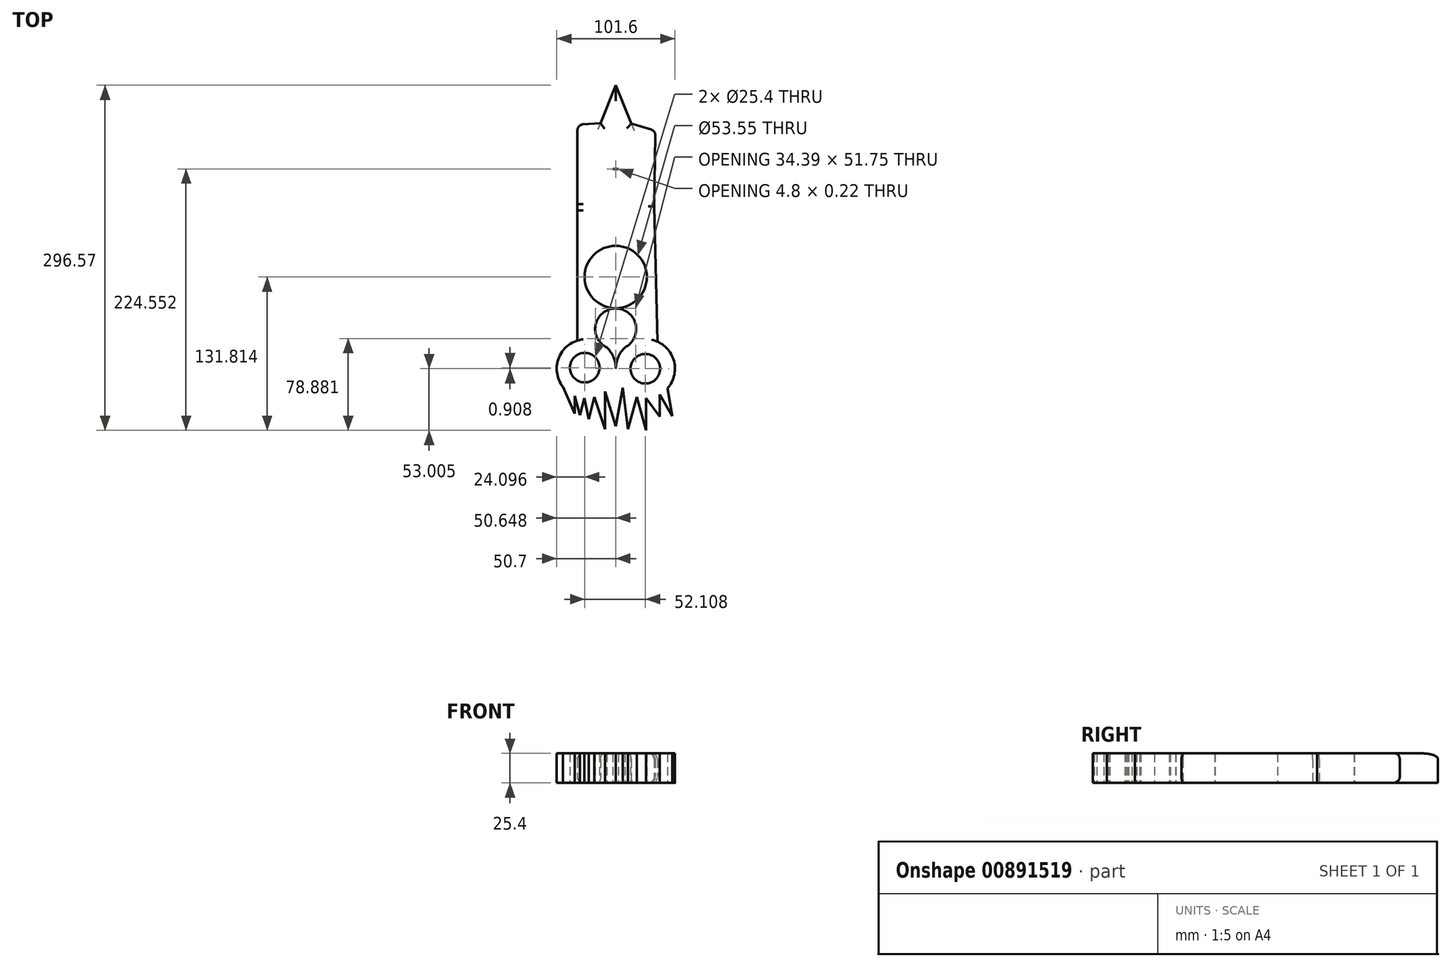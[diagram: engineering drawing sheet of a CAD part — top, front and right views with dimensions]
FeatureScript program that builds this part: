
annotation { "Feature Type Name" : "Feature", "Feature Type Description" : "" }
export const myFeature = defineFeature(function(context is Context, id is Id, definition is map)
    precondition{}
    {
        {
            var Q0;
            Q0=qCreatedBy(makeId("Top.planeOp"),FACE);
            var sketch = newSketch(context, id + "F0", { "sketchPlane" : qUnion([Q0])});
            skCircle(sketch, "E0", {"center": v(-25.3, -34.1) * mm, "radius": 25.4 * mm});
            skCircle(sketch, "E1", {"center": v(25.5, -34.1) * mm, "radius": 25.4 * mm});
            skLineSegment(sketch, "E2", {"start": v(-45.47, -49.53) * mm, "end": v(-35.26, -72.67) * mm});
            skLineSegment(sketch, "E3", {"start": v(-35.26, -72.67) * mm, "end": v(-35.26, -57.47) * mm});
            skLineSegment(sketch, "E4", {"start": v(-35.26, -57.47) * mm, "end": v(-30.65, -73.82) * mm});
            skLineSegment(sketch, "E5", {"start": v(-30.65, -73.82) * mm, "end": v(-27.09, -59.44) * mm});
            skLineSegment(sketch, "E6", {"start": v(-27.09, -59.44) * mm, "end": v(-23.17, -77.56) * mm});
            skLineSegment(sketch, "E7", {"start": v(-23.17, -77.56) * mm, "end": v(-18.39, -58.55) * mm});
            skLineSegment(sketch, "E8", {"start": v(-18.39, -58.55) * mm, "end": v(-9.07, -85.96) * mm});
            skLineSegment(sketch, "E9", {"start": v(-9.07, -85.96) * mm, "end": v(-9.07, -53.64) * mm});
            skLineSegment(sketch, "E10", {"start": v(-9.07, -53.64) * mm, "end": v(0, -83.66) * mm});
            skLineSegment(sketch, "E11", {"start": v(0, -83.66) * mm, "end": v(6.2, -50.61) * mm});
            skLineSegment(sketch, "E12", {"start": v(6.2, -50.61) * mm, "end": v(10.5, -85.96) * mm});
            skLineSegment(sketch, "E13", {"start": v(10.5, -85.96) * mm, "end": v(18.17, -58.42) * mm});
            skLineSegment(sketch, "E14", {"start": v(18.17, -58.42) * mm, "end": v(26.05, -87.11) * mm});
            skLineSegment(sketch, "E15", {"start": v(26.05, -87.11) * mm, "end": v(26.05, -59.5) * mm});
            skLineSegment(sketch, "E16", {"start": v(26.05, -59.5) * mm, "end": v(37.97, -75.12) * mm});
            skLineSegment(sketch, "E17", {"start": v(37.97, -75.12) * mm, "end": v(37.97, -56.24) * mm});
            skLineSegment(sketch, "E18", {"start": v(37.97, -56.24) * mm, "end": v(48.5, -75.02) * mm});
            skLineSegment(sketch, "E19", {"start": v(48.5, -75.02) * mm, "end": v(44.54, -50.92) * mm});
            skCircle(sketch, "E20", {"center": v(0, 0) * mm, "radius": 17.65 * mm});
            skCircle(sketch, "E21", {"center": v(0, 44.7) * mm, "radius": 26.78 * mm});
            skCircle(sketch, "E22", {"center": v(0, 104.57) * mm, "radius": 32.98 * mm});
            skCircle(sketch, "E23", {"center": v(0, 159.25) * mm, "radius": 21.92 * mm});
            skLineSegment(sketch, "E24", {"start": v(-32.86, 107.4) * mm, "end": v(-32.86, -9.86) * mm});
            skLineSegment(sketch, "E25", {"start": v(32.97, 105.4) * mm, "end": v(35.94, -10.95) * mm});
            skLineSegment(sketch, "E26", {"start": v(-13.07, 176.85) * mm, "end": v(0, 209.46) * mm});
            skLineSegment(sketch, "E27", {"start": v(0, 209.46) * mm, "end": v(13.46, 176.55) * mm});
            skLineSegment(sketch, "E28", {"start": v(-32.86, 107.4) * mm, "end": v(-32.86, 175.48) * mm});
            skLineSegment(sketch, "E29", {"start": v(-32.86, 175.48) * mm, "end": v(-13.07, 176.85) * mm});
            skLineSegment(sketch, "E30", {"start": v(13.46, 176.55) * mm, "end": v(34.1, 170.3) * mm});
            skLineSegment(sketch, "E31", {"start": v(34.1, 170.3) * mm, "end": v(32.97, 105.4) * mm});
            skSolve(sketch);
        }
        {
            var Q0;
            Q0 = qSketchRegion(id + "F0", true);
            extrude(context, id + "F1", {"entities" : qUnion([Q0]), "depth" : 25.4 * mm, "offsetDistance" : 25.4 * mm});
        }
        {
            var Q0;
            Q0=makeQuery(id+"F1.opExtrude","CAP_EDGE",EDGE,{"disambiguationData":[OSD([sQuery(id+"F0.wireOp",EDGE,"E31")])],"isStart":false});
            var Q1;
            Q1=makeQuery(id+"F1.opExtrude","CAP_EDGE",EDGE,{"disambiguationData":[OSD([sQuery(id+"F0.wireOp",EDGE,"E31")])],"isStart":true});
            fillet(context, id + "F2", {"entities" : qUnion([Q0, Q1]), "radius" : 5.08 * mm, "tangentPropagation" : true, "allowEdgeOverflow" : false});
        }
        {
            var Q0;
            {var subQ0=sQuery(id+"F0.wireOp",EDGE,"E24");var subQ1=sQuery(id+"F0.wireOp",EDGE,"E22");Q0=makeQuery(id+"F1.opExtrude","CAP_EDGE",EDGE,{"disambiguationData":[OSD([subQ1]),TDD([makeQuery(id+"F0.imprint","IMPRINT",EDGE,{"disambiguationData":[TD([[makeQuery(id+"F0.imprint","INTERSECT",VERTEX,{"derivedFrom":[subQ1,subQ0]}),1.0]])],"derivedFrom":subQ1})])],"isStart":false});}
            var Q1;
            {var subQ0=sQuery(id+"F0.wireOp",EDGE,"E24");var subQ1=sQuery(id+"F0.wireOp",EDGE,"E22");Q1=makeQuery(id+"F1.opExtrude","CAP_EDGE",EDGE,{"disambiguationData":[OSD([subQ1]),TDD([makeQuery(id+"F0.imprint","IMPRINT",EDGE,{"disambiguationData":[TD([[makeQuery(id+"F0.imprint","INTERSECT",VERTEX,{"derivedFrom":[subQ1,subQ0]}),1.0]])],"derivedFrom":subQ1})])],"isStart":true});}
            fillet(context, id + "F3", {"entities" : qUnion([Q0, Q1]), "radius" : 5.08 * mm, "tangentPropagation" : true, "allowEdgeOverflow" : false});
        }
        {
            var Q0;
            Q0=makeQuery(id+"F1.opExtrude","CAP_EDGE",EDGE,{"disambiguationData":[OSD([sQuery(id+"F0.wireOp",EDGE,"E26")])],"isStart":false});
            var Q1;
            Q1=makeQuery(id+"F1.opExtrude","CAP_EDGE",EDGE,{"disambiguationData":[OSD([sQuery(id+"F0.wireOp",EDGE,"E27")])],"isStart":false});
            fillet(context, id + "F4", {"entities" : qUnion([Q0, Q1]), "radius" : 5.08 * mm, "tangentPropagation" : true, "allowEdgeOverflow" : false});
        }
        {
            var Q0;
            Q0=makeQuery(id+"F1.opExtrude","CAP_EDGE",EDGE,{"disambiguationData":[OSD([sQuery(id+"F0.wireOp",EDGE,"E30")])],"isStart":false});
            var Q1;
            Q1=makeQuery(id+"F1.opExtrude","CAP_EDGE",EDGE,{"disambiguationData":[OSD([sQuery(id+"F0.wireOp",EDGE,"E29")])],"isStart":false});
            fillet(context, id + "F5", {"entities" : qUnion([Q0, Q1]), "radius" : 5.08 * mm, "tangentPropagation" : true, "allowEdgeOverflow" : false});
        }
        {
            var Q0;
            Q0=makeQuery(id+"F1.opExtrude","CAP_FACE",FACE,{"disambiguationData":[OSD([sQuery(id+"F0.wireOp",EDGE,"E0"),sQuery(id+"F0.wireOp",EDGE,"E1"),sQuery(id+"F0.wireOp",EDGE,"E2"),sQuery(id+"F0.wireOp",EDGE,"E3"),sQuery(id+"F0.wireOp",EDGE,"E4"),sQuery(id+"F0.wireOp",EDGE,"E5"),sQuery(id+"F0.wireOp",EDGE,"E6"),sQuery(id+"F0.wireOp",EDGE,"E7"),sQuery(id+"F0.wireOp",EDGE,"E8"),sQuery(id+"F0.wireOp",EDGE,"E9"),sQuery(id+"F0.wireOp",EDGE,"E10"),sQuery(id+"F0.wireOp",EDGE,"E11"),sQuery(id+"F0.wireOp",EDGE,"E12"),sQuery(id+"F0.wireOp",EDGE,"E13"),sQuery(id+"F0.wireOp",EDGE,"E14"),sQuery(id+"F0.wireOp",EDGE,"E15"),sQuery(id+"F0.wireOp",EDGE,"E16"),sQuery(id+"F0.wireOp",EDGE,"E17"),sQuery(id+"F0.wireOp",EDGE,"E18"),sQuery(id+"F0.wireOp",EDGE,"E19"),sQuery(id+"F0.wireOp",EDGE,"E20"),sQuery(id+"F0.wireOp",EDGE,"E21"),sQuery(id+"F0.wireOp",EDGE,"E22"),sQuery(id+"F0.wireOp",EDGE,"E23"),sQuery(id+"F0.wireOp",EDGE,"E24"),sQuery(id+"F0.wireOp",EDGE,"E25"),sQuery(id+"F0.wireOp",EDGE,"E26"),sQuery(id+"F0.wireOp",EDGE,"E27"),sQuery(id+"F0.wireOp",EDGE,"E28"),sQuery(id+"F0.wireOp",EDGE,"E29"),sQuery(id+"F0.wireOp",EDGE,"E30"),sQuery(id+"F0.wireOp",EDGE,"E31")])],"isStart":true});
            var sketch = newSketch(context, id + "F6", { "sketchPlane" : qUnion([Q0])});
            skPoint(sketch, "E32", {"position": v(-26.6, 33.2) * mm});
            skPoint(sketch, "E33", {"position": v(25.5, 34.1) * mm});
            skSolve(sketch);
        }
        {
            var Q0;
            Q0=sQuery(id+"F6.wireOp",VERTEX,"E32");
            var Q1;
            Q1=sQuery(id+"F6.wireOp",VERTEX,"E33");
            var Q2;
            Q2=makeQuery(id+"F1.opExtrude","SWEPT_BODY",BODY,{"disambiguationData":[OSD([sQuery(id+"F0.wireOp",EDGE,"E0"),sQuery(id+"F0.wireOp",EDGE,"E1"),sQuery(id+"F0.wireOp",EDGE,"E2"),sQuery(id+"F0.wireOp",EDGE,"E3"),sQuery(id+"F0.wireOp",EDGE,"E4"),sQuery(id+"F0.wireOp",EDGE,"E5"),sQuery(id+"F0.wireOp",EDGE,"E6"),sQuery(id+"F0.wireOp",EDGE,"E7"),sQuery(id+"F0.wireOp",EDGE,"E8"),sQuery(id+"F0.wireOp",EDGE,"E9"),sQuery(id+"F0.wireOp",EDGE,"E10"),sQuery(id+"F0.wireOp",EDGE,"E11"),sQuery(id+"F0.wireOp",EDGE,"E12"),sQuery(id+"F0.wireOp",EDGE,"E13"),sQuery(id+"F0.wireOp",EDGE,"E14"),sQuery(id+"F0.wireOp",EDGE,"E15"),sQuery(id+"F0.wireOp",EDGE,"E16"),sQuery(id+"F0.wireOp",EDGE,"E17"),sQuery(id+"F0.wireOp",EDGE,"E18"),sQuery(id+"F0.wireOp",EDGE,"E19"),sQuery(id+"F0.wireOp",EDGE,"E20"),sQuery(id+"F0.wireOp",EDGE,"E21"),sQuery(id+"F0.wireOp",EDGE,"E22"),sQuery(id+"F0.wireOp",EDGE,"E23"),sQuery(id+"F0.wireOp",EDGE,"E24"),sQuery(id+"F0.wireOp",EDGE,"E25"),sQuery(id+"F0.wireOp",EDGE,"E26"),sQuery(id+"F0.wireOp",EDGE,"E27"),sQuery(id+"F0.wireOp",EDGE,"E28"),sQuery(id+"F0.wireOp",EDGE,"E29"),sQuery(id+"F0.wireOp",EDGE,"E30"),sQuery(id+"F0.wireOp",EDGE,"E31")])]});
            hole(context, id + "F7", {"style" : HoleStyle.SIMPLE, "endStyle" : HoleEndStyle.THROUGH, "holeDiameter" : 25.4 * mm, "majorDiameter" : 6.35 * mm, "isTappedThrough" : true, "tappedDepth" : 12.7 * mm, "tapClearance" : 3, "locations" : qUnion([Q0, Q1]), "scope" : qUnion([Q2])});
        }
    });
